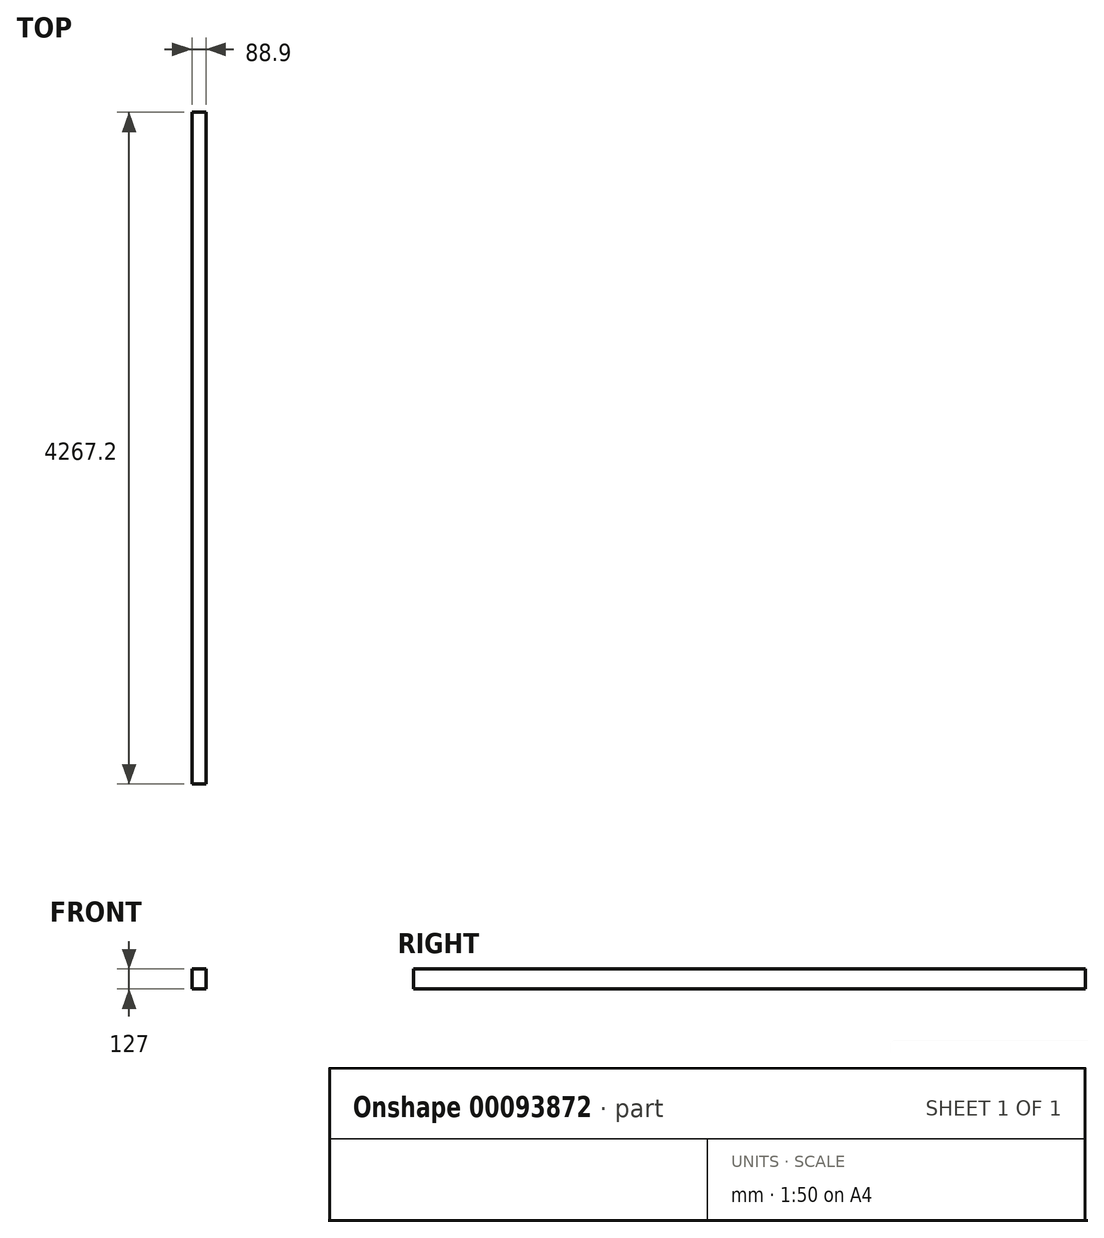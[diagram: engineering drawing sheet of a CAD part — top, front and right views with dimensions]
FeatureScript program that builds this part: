
annotation { "Feature Type Name" : "Feature", "Feature Type Description" : "" }
export const myFeature = defineFeature(function(context is Context, id is Id, definition is map)
    precondition{}
    {
        {
            var Q0;
            Q0=qCreatedBy(makeId("Front.planeOp"),FACE);
            var sketch = newSketch(context, id + "F0", { "sketchPlane" : qUnion([Q0])});
            skLineSegment(sketch, "E0.bottom", {"start": v(0, 0) * mm, "end": v(88.9, 0) * mm});
            skLineSegment(sketch, "E0.top", {"start": v(0, 127) * mm, "end": v(88.9, 127) * mm});
            skLineSegment(sketch, "E0.left", {"start": v(0, 0) * mm, "end": v(0, 127) * mm});
            skLineSegment(sketch, "E0.right", {"start": v(88.9, 0) * mm, "end": v(88.9, 127) * mm});
            skSolve(sketch);
        }
        {
            var Q0;
            Q0 = qSketchRegion(id + "F0", true);
            extrude(context, id + "F1", {"entities" : qUnion([Q0]), "depth" : 4267.2 * mm});
        }
    });
